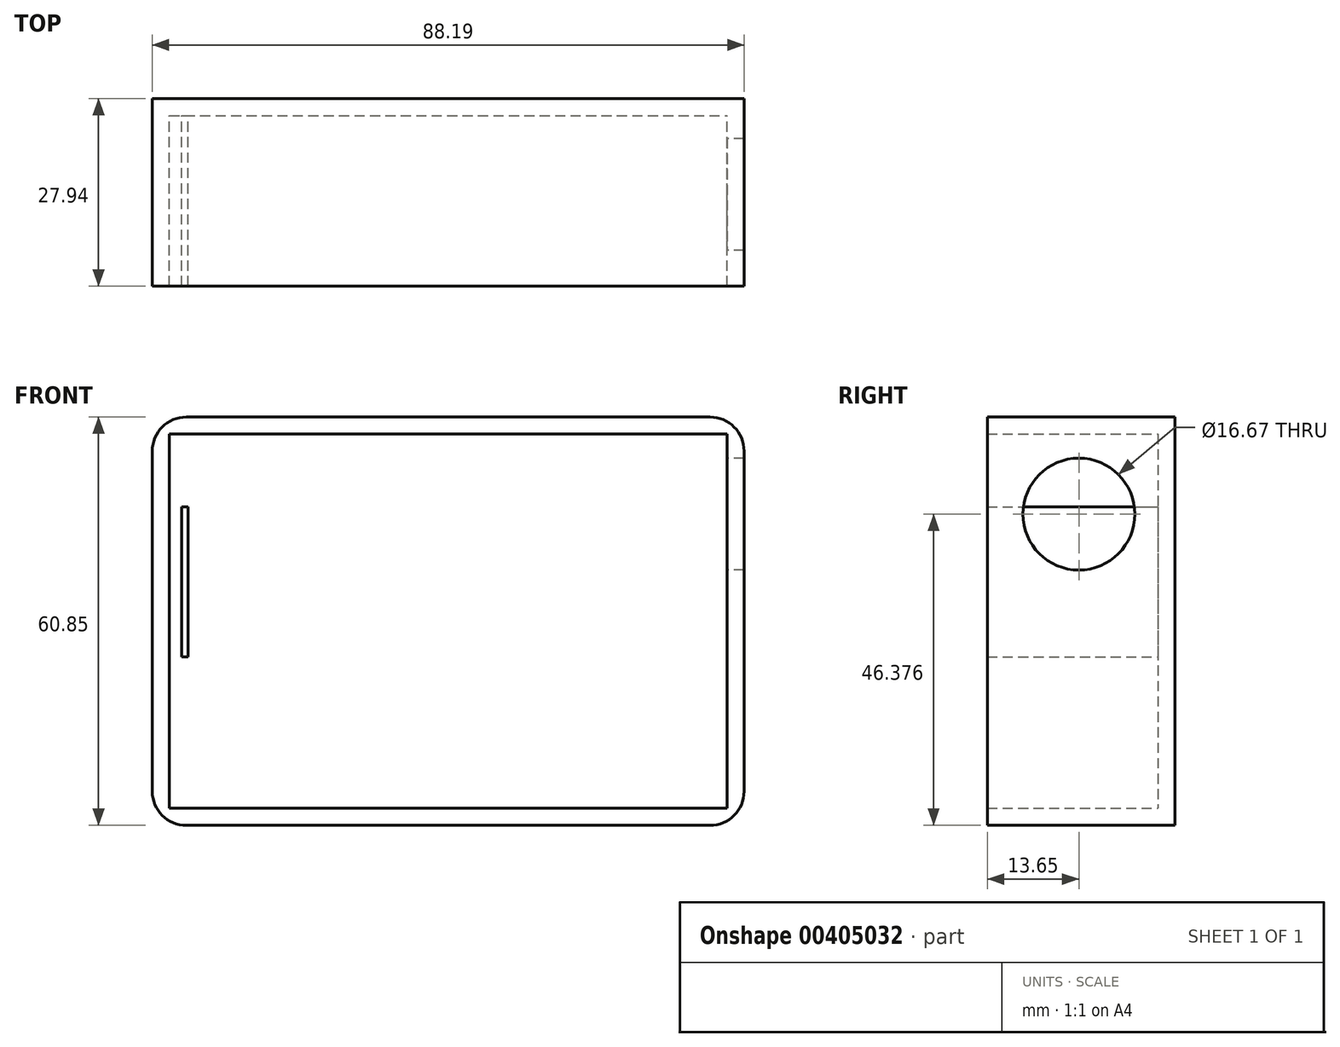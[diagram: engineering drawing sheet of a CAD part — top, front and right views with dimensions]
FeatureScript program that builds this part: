
annotation { "Feature Type Name" : "Feature", "Feature Type Description" : "" }
export const myFeature = defineFeature(function(context is Context, id is Id, definition is map)
    precondition{}
    {
        {
            var Q0;
            Q0=qCreatedBy(makeId("Front.planeOp"),FACE);
            var sketch = newSketch(context, id + "F0", { "sketchPlane" : qUnion([Q0])});
            skLineSegment(sketch, "E0.bottom", {"start": v(-29.16, 19.32) * mm, "end": v(53.95, 19.32) * mm});
            skLineSegment(sketch, "E0.top", {"start": v(-29.16, -36.45) * mm, "end": v(53.95, -36.45) * mm});
            skLineSegment(sketch, "E0.left", {"start": v(-29.16, 19.32) * mm, "end": v(-29.16, -36.45) * mm});
            skLineSegment(sketch, "E0.right", {"start": v(53.95, 19.32) * mm, "end": v(53.95, -36.45) * mm});
            skSolve(sketch);
        }
        {
            var Q0;
            Q0 = qSketchRegion(id + "F0", true);
            extrude(context, id + "F1", {"entities" : qUnion([Q0]), "depth" : 25.4 * mm});
        }
        {
            var Q0;
            Q0=makeQuery(id+"F1.opExtrude","CAP_FACE",FACE,{"disambiguationData":[OSD([sQuery(id+"F0.wireOp",EDGE,"E0.bottom"),sQuery(id+"F0.wireOp",EDGE,"E0.top"),sQuery(id+"F0.wireOp",EDGE,"E0.left"),sQuery(id+"F0.wireOp",EDGE,"E0.right")])],"isStart":false});
            shell(context, id + "F2", {"entities" : qUnion([Q0]), "thickness" : 2.54 * mm, "oppositeDirection" : true});
        }
        {
            var Q0;
            Q0=makeQuery(id+"F1.opExtrude","SWEPT_EDGE",EDGE,{"disambiguationData":[OSD([sQuery(id+"F0.wireOp",EDGE,"E0.top"),sQuery(id+"F0.wireOp",EDGE,"E0.left")])]});
            var Q1;
            Q1=makeQuery(id+"F1.opExtrude","SWEPT_EDGE",EDGE,{"disambiguationData":[OSD([sQuery(id+"F0.wireOp",EDGE,"E0.bottom"),sQuery(id+"F0.wireOp",EDGE,"E0.left")])]});
            var Q2;
            Q2=makeQuery(id+"F1.opExtrude","SWEPT_EDGE",EDGE,{"disambiguationData":[OSD([sQuery(id+"F0.wireOp",EDGE,"E0.top"),sQuery(id+"F0.wireOp",EDGE,"E0.right")])]});
            var Q3;
            Q3=makeQuery(id+"F1.opExtrude","SWEPT_EDGE",EDGE,{"disambiguationData":[OSD([sQuery(id+"F0.wireOp",EDGE,"E0.bottom"),sQuery(id+"F0.wireOp",EDGE,"E0.right")])]});
            fillet(context, id + "F3", {"entities" : qUnion([Q0, Q1, Q2, Q3]), "radius" : 5.08 * mm, "tangentPropagation" : true, "allowEdgeOverflow" : false});
        }
        {
            var Q0;
            Q0=qCreatedBy(makeId("Right.planeOp"),FACE);
            var sketch = newSketch(context, id + "F4", { "sketchPlane" : qUnion([Q0])});
            skCircle(sketch, "E1", {"center": v(-11.75, 7.39) * mm, "radius": 8.34 * mm});
            skSolve(sketch);
        }
        {
            var Q0;
            Q0=sQuery(id+"F4.wireOp",VERTEX,"E1.center");
            var Q1;
            Q1=makeQuery(id+"F1.opExtrude","SWEPT_BODY",BODY,{"disambiguationData":[OSD([sQuery(id+"F0.wireOp",EDGE,"E0.bottom"),sQuery(id+"F0.wireOp",EDGE,"E0.top"),sQuery(id+"F0.wireOp",EDGE,"E0.left"),sQuery(id+"F0.wireOp",EDGE,"E0.right")])]});
            hole(context, id + "F5", {"style" : HoleStyle.SIMPLE, "endStyle" : HoleEndStyle.THROUGH, "oppositeDirection" : true, "standardTappedOrClearance" : lookupTablePath({ "standard" : "ANSI", "fit" : "Normal (ASME)", "size" : "5/8", "type" : "Clearance" }), "standardBlindInLast" : lookupTablePath({ "fit" : "Free", "standard" : "ANSI", "size" : "5/8", "type" : "Clearance" }), "holeDiameter" : 16.67 * mm, "isTappedThrough" : true, "tappedDepth" : 12.7 * mm, "tapClearance" : 3, "locations" : qUnion([Q0]), "scope" : qUnion([Q1])});
        }
        {
            var Q0;
            Q0=qCreatedBy(makeId("Front.planeOp"),FACE);
            var sketch = newSketch(context, id + "F6", { "sketchPlane" : qUnion([Q0])});
            skLineSegment(sketch, "E2.bottom", {"start": v(-27.3, 8.47) * mm, "end": v(-26.36, 8.47) * mm});
            skLineSegment(sketch, "E2.top", {"start": v(-27.3, -13.88) * mm, "end": v(-26.36, -13.88) * mm});
            skLineSegment(sketch, "E2.left", {"start": v(-27.3, 8.47) * mm, "end": v(-27.3, -13.88) * mm});
            skLineSegment(sketch, "E2.right", {"start": v(-26.36, 8.47) * mm, "end": v(-26.36, -13.88) * mm});
            skSolve(sketch);
        }
        {
            var Q0;
            Q0 = qSketchRegion(id + "F6", true);
            extrude(context, id + "F7", {"entities" : qUnion([Q0]), "operationType" : NewBodyOperationType.ADD, "depth" : 25.4 * mm});
        }
    });
